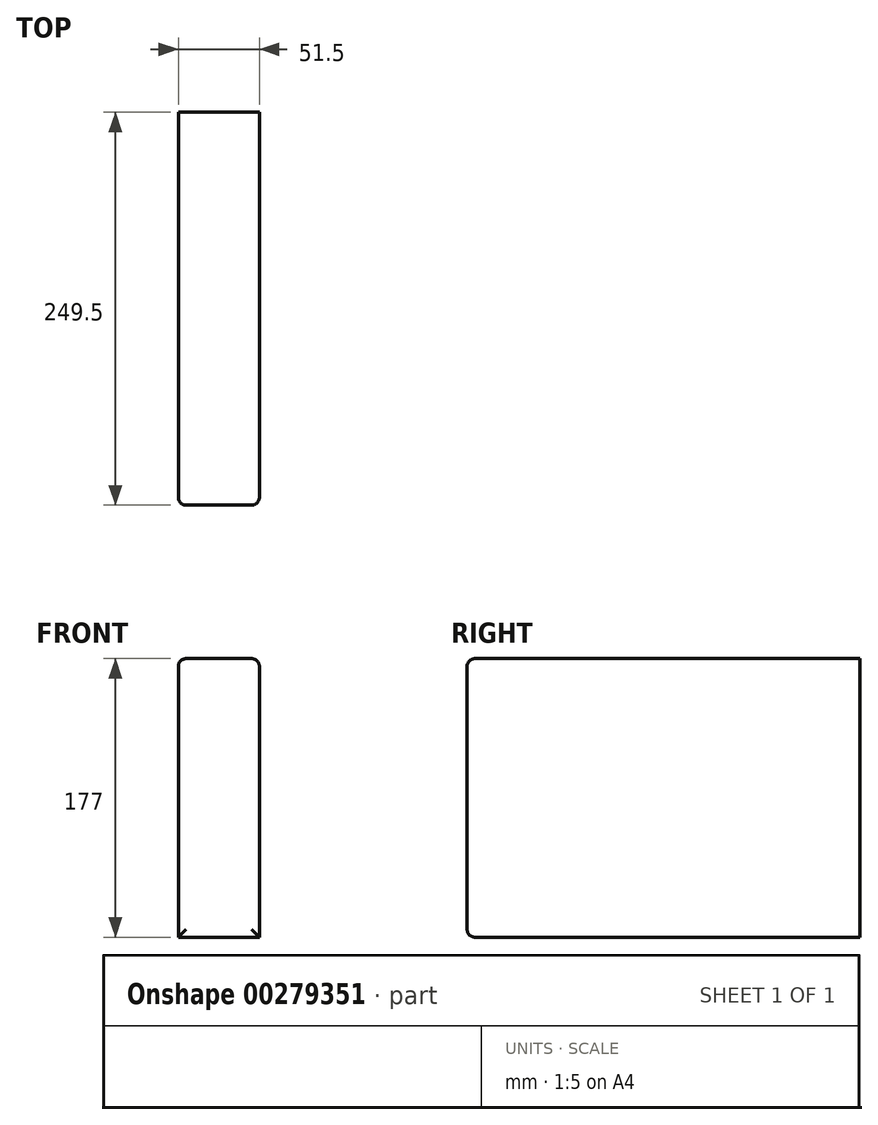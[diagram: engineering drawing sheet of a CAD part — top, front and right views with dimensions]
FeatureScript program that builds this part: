
annotation { "Feature Type Name" : "Feature", "Feature Type Description" : "" }
export const myFeature = defineFeature(function(context is Context, id is Id, definition is map)
    precondition{}
    {
        {
            var Q0;
            Q0=qCreatedBy(makeId("Front.planeOp"),FACE);
            var sketch = newSketch(context, id + "F0", { "sketchPlane" : qUnion([Q0])});
            skLineSegment(sketch, "E0.bottom", {"start": v(25.75, -88.5) * mm, "end": v(-25.75, -88.5) * mm});
            skLineSegment(sketch, "E0.top", {"start": v(25.75, 88.5) * mm, "end": v(-25.75, 88.5) * mm});
            skLineSegment(sketch, "E0.left", {"start": v(25.75, -88.5) * mm, "end": v(25.75, 88.5) * mm});
            skLineSegment(sketch, "E0.right", {"start": v(-25.75, -88.5) * mm, "end": v(-25.75, 88.5) * mm});
            skPoint(sketch, "E0.middle", {"position": v(0, 0) * mm});
            skSolve(sketch);
        }
        {
            var Q0;
            Q0=qSketchRegion(id+"F0",true);
            extrude(context, id + "F1", {"entities" : qUnion([Q0]), "depth" : 249.5 * mm, "symmetric" : true});
        }
        {
            var Q0;
            Q0=makeQuery(id+"F1.opExtrude","CAP_EDGE",EDGE,{"disambiguationData":[OSD([sQuery(id+"F0.wireOp",EDGE,"E0.top")])],"isStart":false});
            fillet(context, id + "F2", {"entities" : qUnion([Q0]), "radius" : 5 * mm, "tangentPropagation" : true, "allowEdgeOverflow" : false});
        }
        {
            var Q0;
            Q0=makeQuery(id+"F1.opExtrude","CAP_FACE",FACE,{"disambiguationData":[OSD([sQuery(id+"F0.wireOp",EDGE,"E0.bottom"),sQuery(id+"F0.wireOp",EDGE,"E0.top"),sQuery(id+"F0.wireOp",EDGE,"E0.left"),sQuery(id+"F0.wireOp",EDGE,"E0.right")])],"isStart":false});
            var Q1;
            Q1=makeQuery(id+"F1.opExtrude","CAP_EDGE",EDGE,{"disambiguationData":[OSD([sQuery(id+"F0.wireOp",EDGE,"E0.bottom")])],"isStart":false});
            fillet(context, id + "F3", {"entities" : qUnion([Q0, Q1]), "radius" : 5 * mm, "tangentPropagation" : true, "allowEdgeOverflow" : false});
        }
        {
            var Q0;
            Q0=makeQuery(id+"F1.opExtrude","CAP_FACE",FACE,{"disambiguationData":[OSD([sQuery(id+"F0.wireOp",EDGE,"E0.bottom"),sQuery(id+"F0.wireOp",EDGE,"E0.top"),sQuery(id+"F0.wireOp",EDGE,"E0.left"),sQuery(id+"F0.wireOp",EDGE,"E0.right")])],"isStart":false});
            extrude(context, id + "F4", {"entities" : qUnion([Q0]), "operationType" : NewBodyOperationType.ADD, "oppositeDirection" : true, "depth" : 25 * mm});
        }
        {
            var Q0;
            Q0=makeQuery(id+"F1.opExtrude","CAP_FACE",FACE,{"disambiguationData":[OSD([sQuery(id+"F0.wireOp",EDGE,"E0.bottom"),sQuery(id+"F0.wireOp",EDGE,"E0.top"),sQuery(id+"F0.wireOp",EDGE,"E0.left"),sQuery(id+"F0.wireOp",EDGE,"E0.right")])],"isStart":false});
            extrude(context, id + "F5", {"entities" : qUnion([Q0]), "operationType" : NewBodyOperationType.ADD, "oppositeDirection" : true, "depth" : 40.6 * mm});
        }
    });
